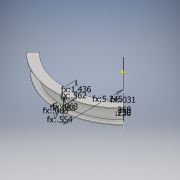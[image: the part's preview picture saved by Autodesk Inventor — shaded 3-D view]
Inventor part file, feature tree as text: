
AUTODESK INVENTOR PART (.ipt)
format: ipt  version: 2017 (Build 210142000, 142)  size: 167,936 bytes
history: native  units: in
note: dims shown in document units (in); Inventor stores cm internally (conversion verified against a paired STEP export)
features: sketch x5, extrude x4, revolve x1, plane x1
ambient origin geometry x8: Origin, YZ Plane, XZ Plane, XY Plane, X Axis, Y Axis, Z Axis, Center Point
bodies: Solid1 (feature_tree)
feature tree (11):
  revolve  "Revolution1"  [1 undecoded]
  plane  "Work Plane1"
  sketch  "Sketch2"  dims[d3=1.4364in d4=0.0625in]
  extrude  "Extrusion2"  Depth=0.0625in
  extrude  "Extrusion3"  TaperAngle=90.0deg  [1 undecoded]
  extrude  "Extrusion4"  Depth=0.375in
  extrude  "Extrusion5"  Depth=0.0312in TaperAngle=0.0deg
  sketch  "Sketch5"  dims[d11=0.3125in d12=1.0in d13=0.0in d14=0.0156in d15=0.0in d16=0.25in d17=0.0625in d18=0.0in d19=135.0deg d20=0.0in d21=0.0in d22=0.75in d23=0.0312in d24=0.25in d25=0.25in]
  sketch  "Sketch1"  dims[d1=0.5536in d2=0.0625in]
  sketch  "Sketch3"  dims[d5=0.0625in d6=90.0deg]
  sketch  "Sketch4"  dims[d7=0.562in d8=0.375in]
note: 2 required parameter values undecoded (feature->parameter linkage not recoverable at this tier; creation-order binding heuristic only, values carry confidence <= 0.55)